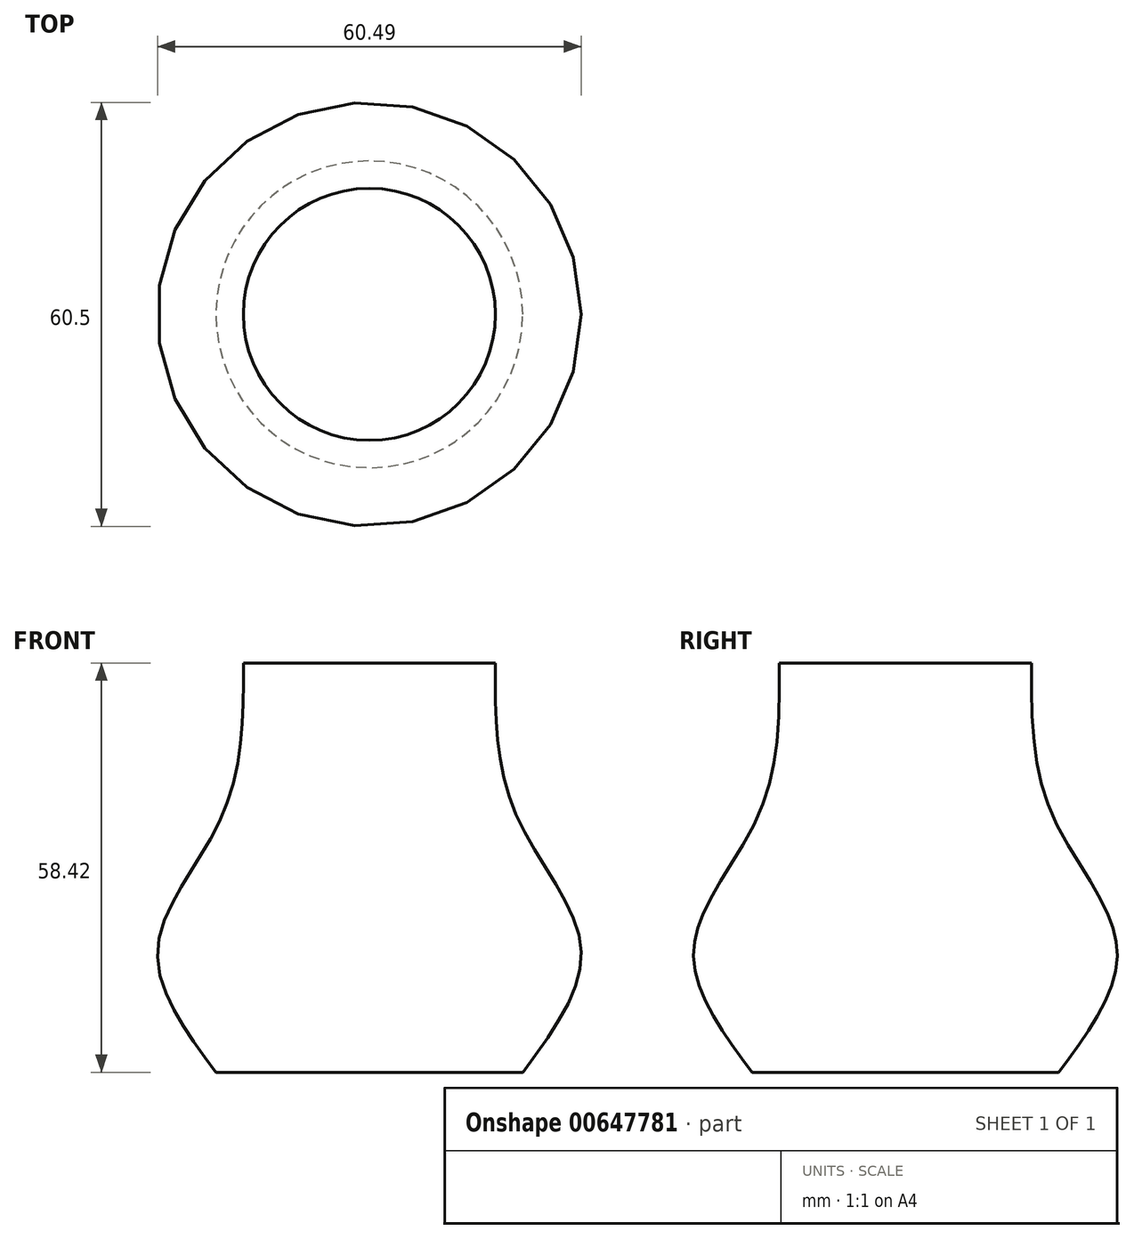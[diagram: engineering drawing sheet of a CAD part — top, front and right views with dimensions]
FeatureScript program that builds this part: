
annotation { "Feature Type Name" : "Feature", "Feature Type Description" : "" }
export const myFeature = defineFeature(function(context is Context, id is Id, definition is map)
    precondition{}
    {
        {
            var Q0;
            Q0=qCreatedBy(makeId("Top.planeOp"),FACE);
            var sketch = newSketch(context, id + "F0", { "sketchPlane" : qUnion([Q0])});
            skCircle(sketch, "E0", {"center": v(0, 0) * mm, "radius": 21.9 * mm});
            skCircle(sketch, "E1", {"center": v(0, 0) * mm, "radius": 25.92 * mm});
            skSolve(sketch);
        }
        {
            var Q0;
            Q0=qCreatedBy(makeId("Top.planeOp"),FACE);
            cPlane(context, id + "F1", {"entities" : qUnion([Q0]), "cplaneType" : CPlaneType.OFFSET, "offset" : 17.27 * mm, "width" : 152.4 * mm, "height" : 152.4 * mm});
        }
        {
            var Q0;
            Q0=qCreatedBy(makeId("Top.planeOp"),FACE);
            cPlane(context, id + "F2", {"entities" : qUnion([Q0]), "cplaneType" : CPlaneType.OFFSET, "offset" : 26.16 * mm, "width" : 152.4 * mm, "height" : 152.4 * mm});
        }
        {
            var Q0;
            Q0=qCreatedBy(id+"F2.planeOp",FACE);
            cPlane(context, id + "F3", {"entities" : qUnion([Q0]), "cplaneType" : CPlaneType.OFFSET, "offset" : 10.4 * mm, "width" : 152.4 * mm, "height" : 152.4 * mm});
        }
        {
            var Q0;
            Q0=qCreatedBy(id+"F3.planeOp",FACE);
            var sketch = newSketch(context, id + "F4", { "sketchPlane" : qUnion([Q0])});
            skCircle(sketch, "E2", {"center": v(0, 0) * mm, "radius": 21.03 * mm});
            skSolve(sketch);
        }
        {
            var Q0;
            Q0=qCreatedBy(id+"F3.planeOp",FACE);
            cPlane(context, id + "F5", {"entities" : qUnion([Q0]), "cplaneType" : CPlaneType.OFFSET, "offset" : 21.84 * mm, "width" : 152.4 * mm, "height" : 152.4 * mm});
        }
        {
            var Q0;
            Q0=qCreatedBy(id+"F5.planeOp",FACE);
            var sketch = newSketch(context, id + "F6", { "sketchPlane" : qUnion([Q0])});
            skCircle(sketch, "E3", {"center": v(0, 0) * mm, "radius": 17.98 * mm});
            skSolve(sketch);
        }
        {
            var Q0;
            Q0=qCreatedBy(id+"F1.planeOp",FACE);
            var sketch = newSketch(context, id + "F7", { "sketchPlane" : qUnion([Q0])});
            skCircle(sketch, "E4", {"center": v(0, 0) * mm, "radius": 30.24 * mm});
            skSolve(sketch);
        }
        {
            var Q0;
            Q0=makeQuery(id+"F0.imprint","IMPRINT",FACE,{"disambiguationData":[TD([[makeQuery(id+"F0.imprint","IMPRINT",EDGE,{"derivedFrom":sQuery(id+"F0.wireOp",EDGE,"E0")}),1.0]])]});
            var Q1;
            Q1=makeQuery(id+"F7.imprint","IMPRINT",FACE,{"disambiguationData":[TD([[makeQuery(id+"F7.imprint","IMPRINT",EDGE,{"derivedFrom":sQuery(id+"F7.wireOp",EDGE,"E4")}),1.0]])]});
            var Q2;
            Q2=makeQuery(id+"F4.imprint","IMPRINT",FACE,{"disambiguationData":[TD([[makeQuery(id+"F4.imprint","IMPRINT",EDGE,{"derivedFrom":sQuery(id+"F4.wireOp",EDGE,"E2")}),1.0]])]});
            var Q3;
            Q3=makeQuery(id+"F6.imprint","IMPRINT",FACE,{"disambiguationData":[TD([[makeQuery(id+"F6.imprint","IMPRINT",EDGE,{"derivedFrom":sQuery(id+"F6.wireOp",EDGE,"E3")}),1.0]])]});
            var Q4;
            Q4=sQuery(id+"F0.wireOp",EDGE,"E0");
            var Q5;
            Q5=sQuery(id+"F7.wireOp",EDGE,"E4");
            var Q6;
            Q6=sQuery(id+"F4.wireOp",EDGE,"E2");
            var Q7;
            Q7=sQuery(id+"F6.wireOp",EDGE,"E3");
            loft(context, id + "F8", {"sheetProfilesArray" : [{ "sheetProfileEntities" : qUnion([Q0]) }, { "sheetProfileEntities" : qUnion([Q1]) }, { "sheetProfileEntities" : qUnion([Q2]) }, { "sheetProfileEntities" : qUnion([Q3]) }], "wireProfilesArray" : [{ "wireProfileEntities" : qUnion([Q4]) }, { "wireProfileEntities" : qUnion([Q5]) }, { "wireProfileEntities" : qUnion([Q6]) }, { "wireProfileEntities" : qUnion([Q7]) }]});
        }
    });
